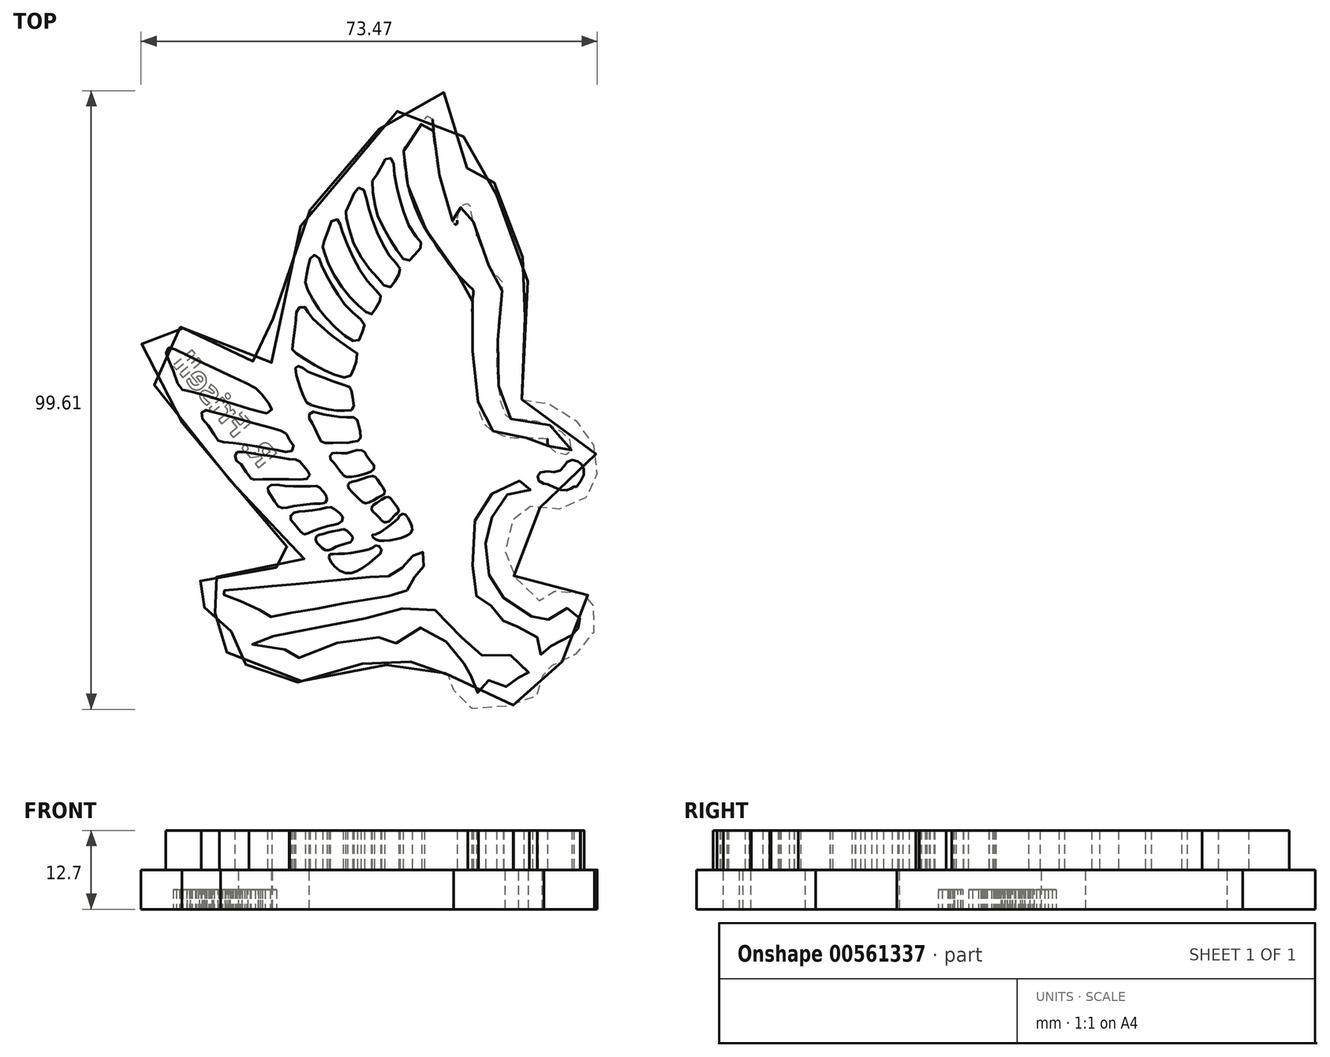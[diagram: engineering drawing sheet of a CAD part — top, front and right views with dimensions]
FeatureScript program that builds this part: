
annotation { "Feature Type Name" : "Feature", "Feature Type Description" : "" }
export const myFeature = defineFeature(function(context is Context, id is Id, definition is map)
    precondition{}
    {
        {
            var Q0;
            Q0=qCreatedBy(makeId("Top.planeOp"),FACE);
            var sketch = newSketch(context, id + "F0", { "sketchPlane" : qUnion([Q0])});
            skFitSpline(sketch, "E0", {"points": [v(-27.46, -3.62) * mm, v(-24.19, -4.03) * mm, v(-19.81, -6.13) * mm, v(-16.66, -9.45) * mm, v(-15.38, -13.42) * mm, v(-15.73, -17.22) * mm, v(-17.6, -19.78) * mm, v(-21.5, -21.24) * mm, v(-25.7, -20.83) * mm, v(-27.34, -21.24) * mm, v(-29.61, -24.4) * mm, v(-29.96, -29.3) * mm, v(-28.04, -32.85) * mm, v(-24.6, -36) * mm, v(-24.54, -35.89) * mm, v(-22.9, -34.72) * mm, v(-19.81, -34.37) * mm, v(-16.43, -35.36) * mm, v(-16.02, -36.35) * mm, v(-15.79, -38.75) * mm, v(-16.49, -42.6) * mm, v(-19.75, -45.17) * mm, v(-22.55, -46.45) * mm, v(-23.72, -46.8) * mm, v(-24.13, -47.8) * mm, v(-23.95, -49.48) * mm, v(-26, -52) * mm, v(-30.72, -53.1) * mm, v(-36.44, -53.16) * mm, v(-38.37, -50.53) * mm, v(-38.54, -48.43) * mm, v(-39.65, -47.8) * mm, v(-41.87, -45.75) * mm, v(-42.4, -44.82) * mm, v(-43.97, -45.05) * mm, v(-45.84, -46.1) * mm, v(-48.52, -46.57) * mm, v(-49.86, -46.1) * mm, v(-51.5, -46.04) * mm, v(-56.05, -46.45) * mm, v(-60.54, -47.67) * mm, v(-63.17, -49.02) * mm, v(-65.2, -48.96) * mm, v(-66.55, -47.73) * mm, v(-70.23, -46.97) * mm, v(-73.79, -45.17) * mm, v(-75.71, -43.47) * mm, v(-75.83, -41.9) * mm, v(-74.37, -40.96) * mm, v(-73.09, -40.44) * mm, v(-73.5, -39.62) * mm, v(-75.95, -38.4) * mm, v(-78.8, -37) * mm, v(-81.5, -35.3) * mm, v(-82.2, -33.96) * mm, v(-81.2, -33.38) * mm, v(-77.64, -32.39) * mm, v(-72.62, -31.45) * mm, v(-66.73, -30.64) * mm, v(-61.77, -29.94) * mm, v(-61.77, -29.76) * mm, v(-63.34, -28.77) * mm, v(-66.61, -25.97) * mm, v(-70.35, -21.12) * mm, v(-73.85, -17.27) * mm, v(-77.76, -12.72) * mm, v(-81.96, -7.53) * mm, v(-86.22, -2.1) * mm, v(-88.67, 5.2) * mm, v(-88.38, 8.17) * mm, v(-86.45, 9.16) * mm, v(-82.43, 8.05) * mm, v(-77.3, 5.72) * mm, v(-72.27, 3.27) * mm, v(-69, 2.04) * mm, v(-67.72, 2.4) * mm, v(-67.72, 4.78) * mm, v(-66.55, 15) * mm, v(-62.06, 26.14) * mm, v(-55.53, 34.55) * mm, v(-49.05, 41.37) * mm, v(-43.91, 45.45) * mm, v(-40.35, 45.98) * mm, v(-38.54, 44.29) * mm, v(-36.85, 38.8) * mm, v(-35.92, 32.03) * mm, v(-35.57, 32.2) * mm, v(-34.16, 34.37) * mm, v(-32.3, 32.56) * mm, v(-30.72, 25.09) * mm, v(-28.15, 20.25) * mm, v(-26.87, 18.73) * mm, v(-26.4, 17.74) * mm, v(-26.58, 14.59) * mm, v(-27.1, 7.53) * mm, v(-27.92, -0.47) * mm, v(-27.46, -3.62) * mm]});
            skSolve(sketch);
        }
        {
            var Q0;
            Q0 = qSketchRegion(id + "F0", true);
            extrude(context, id + "F1", {"entities" : qUnion([Q0]), "oppositeDirection" : true, "depth" : 6.35 * mm, "offsetDistance" : 25.4 * mm});
        }
        {
            var Q0;
            Q0=qCreatedBy(makeId("Top.planeOp"),FACE);
            var sketch = newSketch(context, id + "F2", { "sketchPlane" : qUnion([Q0])});
            skFitSpline(sketch, "E1", {"points": [v(-51.04, -25.31) * mm, v(-51.52, -25.35) * mm, v(-51.52, -25.66) * mm, v(-51.02, -26.1) * mm, v(-50.3, -26.34) * mm, v(-48.86, -26.31) * mm, v(-47.17, -25.97) * mm, v(-45.9, -25.5) * mm, v(-45.17, -24.78) * mm, v(-45.15, -24.02) * mm, v(-45.57, -23.09) * mm, v(-46.1, -22.25) * mm, v(-46.47, -22) * mm, v(-47.1, -22.22) * mm, v(-47.35, -22.7) * mm, v(-48.04, -23.34) * mm, v(-49.27, -24.27) * mm, v(-51.04, -25.31) * mm]});
            skFitSpline(sketch, "E2", {"points": [v(-50.45, -22.6) * mm, v(-49.82, -23.24) * mm, v(-49.4, -23.4) * mm, v(-48.9, -23.23) * mm, v(-48.23, -22.57) * mm, v(-47.83, -22.14) * mm, v(-47.45, -21.88) * mm, v(-47.28, -21.48) * mm, v(-47.79, -20.59) * mm, v(-48.48, -19.66) * mm, v(-48.92, -19.3) * mm, v(-49.42, -19.34) * mm, v(-51.03, -20.37) * mm, v(-51.5, -20.73) * mm, v(-51.69, -21.2) * mm, v(-51.41, -21.69) * mm, v(-50.45, -22.6) * mm]});
            skFitSpline(sketch, "E3", {"points": [v(-54.05, -16.7) * mm, v(-54.96, -16.88) * mm, v(-55.42, -17.2) * mm, v(-55.48, -17.65) * mm, v(-54.82, -18.46) * mm, v(-53.58, -19.71) * mm, v(-52.94, -20.23) * mm, v(-52.37, -20.3) * mm, v(-51.26, -19.77) * mm, v(-50.08, -19.1) * mm, v(-49.6, -18.83) * mm, v(-49.59, -18.2) * mm, v(-50.1, -17.36) * mm, v(-50.9, -16.28) * mm, v(-51.3, -15.92) * mm, v(-52.13, -16.03) * mm, v(-54.05, -16.7) * mm]});
            skFitSpline(sketch, "E4", {"points": [v(-57.72, -13.85) * mm, v(-56.93, -14.86) * mm, v(-56.26, -15.72) * mm, v(-55.94, -16.02) * mm, v(-55.52, -16.07) * mm, v(-53.9, -15.92) * mm, v(-52.14, -15.37) * mm, v(-51.39, -14.9) * mm, v(-51.2, -14.4) * mm, v(-51.52, -13.84) * mm, v(-52.48, -12.6) * mm, v(-52.8, -12.02) * mm, v(-53.23, -11.8) * mm, v(-54.23, -11.79) * mm, v(-55.3, -12.15) * mm, v(-56.3, -12.28) * mm, v(-57.4, -12.16) * mm, v(-58.09, -12.3) * mm, v(-58.3, -12.63) * mm, v(-58.28, -13.2) * mm, v(-57.72, -13.85) * mm]});
            skFitSpline(sketch, "E5", {"points": [v(-60.74, -8.34) * mm, v(-60, -9.95) * mm, v(-59.7, -10.42) * mm, v(-59, -10.58) * mm, v(-56.88, -10.55) * mm, v(-55.63, -10.57) * mm, v(-54.74, -10.42) * mm, v(-53.93, -10.3) * mm, v(-53.49, -9.95) * mm, v(-53.46, -8.76) * mm, v(-53.79, -7.67) * mm, v(-53.94, -6.97) * mm, v(-54.45, -6.5) * mm, v(-55.99, -6.45) * mm, v(-57.67, -6.27) * mm, v(-59.4, -6.02) * mm, v(-60.52, -5.7) * mm, v(-61.18, -5.58) * mm, v(-61.67, -5.94) * mm, v(-61.74, -6.5) * mm, v(-61.22, -7.41) * mm, v(-60.74, -8.34) * mm]});
            skFitSpline(sketch, "E6", {"points": [v(-63.17, -1.71) * mm, v(-62.41, -3.58) * mm, v(-61.93, -4.24) * mm, v(-60.58, -4.72) * mm, v(-58.33, -5.25) * mm, v(-56.8, -5.38) * mm, v(-55.13, -5.36) * mm, v(-54.57, -5.03) * mm, v(-54.67, -3.39) * mm, v(-54.87, -2.14) * mm, v(-55.05, -1.69) * mm, v(-56.2, -1.23) * mm, v(-58.7, -0.34) * mm, v(-60.9, 0.47) * mm, v(-62.36, 1.16) * mm, v(-62.93, 1.64) * mm, v(-63.62, 1.76) * mm, v(-63.88, 1.6) * mm, v(-63.87, 0.57) * mm, v(-63.37, -1.03) * mm, v(-63.17, -1.71) * mm]});
            skFitSpline(sketch, "E7", {"points": [v(-54.52, 1.42) * mm, v(-54.96, 0.35) * mm, v(-55.57, -0.04) * mm, v(-57.39, 0.32) * mm, v(-59.4, 1.18) * mm, v(-61.74, 2.53) * mm, v(-63.58, 3.67) * mm, v(-64.25, 4.2) * mm, v(-64.47, 4.66) * mm, v(-64.2, 6.39) * mm, v(-63.9, 8.7) * mm, v(-63.81, 10.1) * mm, v(-63.62, 10.9) * mm, v(-63.15, 11.33) * mm, v(-62.5, 11.33) * mm, v(-62.08, 10.92) * mm, v(-61.72, 10.1) * mm, v(-60.7, 9.02) * mm, v(-58.33, 6.9) * mm, v(-56.27, 5.4) * mm, v(-54.17, 3.97) * mm, v(-53.97, 3.78) * mm, v(-54.19, 2.21) * mm, v(-54.52, 1.42) * mm]});
            skFitSpline(sketch, "E8", {"points": [v(-53.17, 7.17) * mm, v(-53.61, 6.04) * mm, v(-54.24, 5.74) * mm, v(-55.3, 6.2) * mm, v(-57.23, 7.79) * mm, v(-59.49, 10.1) * mm, v(-60.67, 11.77) * mm, v(-61.78, 13.77) * mm, v(-62.3, 14.94) * mm, v(-62.29, 15.94) * mm, v(-62.03, 16.96) * mm, v(-61.75, 18.44) * mm, v(-61.5, 19.25) * mm, v(-60.98, 19.66) * mm, v(-60.31, 19.46) * mm, v(-59.98, 18.81) * mm, v(-59.58, 17.76) * mm, v(-58.35, 15.34) * mm, v(-57.3, 13.62) * mm, v(-56.03, 11.73) * mm, v(-54.32, 10.12) * mm, v(-53.09, 9.02) * mm, v(-52.83, 8.32) * mm, v(-53.17, 7.17) * mm]});
            skFitSpline(sketch, "E9", {"points": [v(-51.1, 10.94) * mm, v(-50.37, 12.28) * mm, v(-50.18, 12.7) * mm, v(-50.23, 13.17) * mm, v(-50.7, 13.7) * mm, v(-52.36, 15.53) * mm, v(-53.96, 17.96) * mm, v(-55.32, 20.76) * mm, v(-56.47, 23.7) * mm, v(-56.72, 24.63) * mm, v(-56.85, 25.12) * mm, v(-57.37, 25.47) * mm, v(-58.04, 25.24) * mm, v(-58.45, 24.13) * mm, v(-59.2, 22.13) * mm, v(-59.49, 21.57) * mm, v(-59.49, 20.61) * mm, v(-59.08, 19.57) * mm, v(-58.36, 17.67) * mm, v(-56.85, 15.13) * mm, v(-55.24, 12.97) * mm, v(-53.49, 11.25) * mm, v(-52.4, 10.4) * mm, v(-51.87, 10.1) * mm, v(-51.32, 10.43) * mm, v(-51.1, 10.94) * mm]});
            skFitSpline(sketch, "E10", {"points": [v(-47.94, 15.45) * mm, v(-48.57, 14.55) * mm, v(-49.36, 14.57) * mm, v(-50.53, 15.76) * mm, v(-52.54, 18.15) * mm, v(-54.84, 22.28) * mm, v(-55.66, 25.43) * mm, v(-55.86, 26.34) * mm, v(-55.25, 27.84) * mm, v(-54.36, 29.83) * mm, v(-53.78, 30.45) * mm, v(-53.22, 30.45) * mm, v(-52.64, 29.46) * mm, v(-52.2, 27.4) * mm, v(-51.34, 24.8) * mm, v(-49.85, 21.36) * mm, v(-48.27, 18.91) * mm, v(-47.28, 17.9) * mm, v(-47.06, 17.28) * mm, v(-47.25, 16.55) * mm, v(-47.94, 15.45) * mm]});
            skFitSpline(sketch, "E11", {"points": [v(-44.82, 19.6) * mm, v(-45.48, 18.86) * mm, v(-46.16, 18.78) * mm, v(-47.34, 20.09) * mm, v(-48.86, 22.43) * mm, v(-50.65, 25.95) * mm, v(-51.2, 28.1) * mm, v(-51.55, 31.43) * mm, v(-51.12, 32.12) * mm, v(-50.1, 33.9) * mm, v(-49.5, 34.98) * mm, v(-49, 35.37) * mm, v(-48.3, 35.06) * mm, v(-48.09, 33.9) * mm, v(-47.74, 31.23) * mm, v(-47.05, 28.49) * mm, v(-45.78, 24.66) * mm, v(-44.08, 22.13) * mm, v(-43.66, 21.62) * mm, v(-43.7, 20.98) * mm, v(-44.82, 19.6) * mm]});
            skFitSpline(sketch, "E12", {"points": [v(-52.13, -27.7) * mm, v(-51.3, -27.36) * mm, v(-50.95, -27.1) * mm, v(-50.4, -27.27) * mm, v(-50.06, -28) * mm, v(-50.76, -28.87) * mm, v(-53.08, -30.72) * mm, v(-54.62, -31.45) * mm, v(-56.24, -31.48) * mm, v(-57.8, -30.29) * mm, v(-58.44, -29.37) * mm, v(-58.43, -28.57) * mm, v(-58.1, -28.52) * mm, v(-57.08, -28.47) * mm, v(-55.42, -28.35) * mm, v(-53.4, -28) * mm, v(-52.13, -27.7) * mm]});
            skFitSpline(sketch, "E13", {"points": [v(-59.1, -27.87) * mm, v(-59.93, -27.2) * mm, v(-60.61, -26.42) * mm, v(-60.54, -25.66) * mm, v(-59.82, -25.33) * mm, v(-58.06, -24.88) * mm, v(-56.6, -24.57) * mm, v(-56.03, -24.51) * mm, v(-54.92, -25.42) * mm, v(-54.7, -26.04) * mm, v(-55.07, -26.56) * mm, v(-56.82, -27.1) * mm, v(-58.3, -27.8) * mm, v(-59.1, -27.87) * mm]});
            skFitSpline(sketch, "E14", {"points": [v(-64.2, -23.56) * mm, v(-64.74, -22.83) * mm, v(-64.53, -22.1) * mm, v(-63.6, -21.71) * mm, v(-62.07, -21.56) * mm, v(-59.49, -21.15) * mm, v(-58.3, -20.93) * mm, v(-57.58, -21.27) * mm, v(-56.4, -22.36) * mm, v(-56.32, -23) * mm, v(-57.05, -23.59) * mm, v(-58.24, -23.87) * mm, v(-60.5, -24.59) * mm, v(-61.96, -25.16) * mm, v(-62.58, -25.27) * mm, v(-63.47, -24.42) * mm, v(-64.2, -23.56) * mm]});
            skFitSpline(sketch, "E15", {"points": [v(-59.49, -18.43) * mm, v(-58.93, -19.13) * mm, v(-58.91, -19.95) * mm, v(-59.34, -20.3) * mm, v(-60.75, -20.38) * mm, v(-64.47, -20.82) * mm, v(-65.78, -21.1) * mm, v(-66.57, -20.9) * mm, v(-67.54, -19.53) * mm, v(-68.27, -18.45) * mm, v(-68.37, -17.85) * mm, v(-67.87, -17.38) * mm, v(-66.1, -17.44) * mm, v(-63.05, -17.59) * mm, v(-60.73, -17.53) * mm, v(-60.19, -17.62) * mm, v(-59.49, -18.43) * mm]});
            skFitSpline(sketch, "E16", {"points": [v(-62.65, -14.29) * mm, v(-61.82, -15.2) * mm, v(-61.6, -15.67) * mm, v(-61.93, -16.33) * mm, v(-63.34, -16.47) * mm, v(-67.87, -16.45) * mm, v(-70.59, -16.49) * mm, v(-70.9, -16.43) * mm, v(-71.67, -15.57) * mm, v(-73.02, -13.69) * mm, v(-73.56, -13.35) * mm, v(-73.6, -12.41) * mm, v(-73.33, -12.09) * mm, v(-72.21, -12.09) * mm, v(-70.23, -12.4) * mm, v(-67.5, -12.78) * mm, v(-64.98, -13.18) * mm, v(-63.81, -13.3) * mm, v(-63.2, -13.6) * mm, v(-62.65, -14.29) * mm]});
            skFitSpline(sketch, "E17", {"points": [v(-66.86, -11.75) * mm, v(-65.25, -12.05) * mm, v(-64.44, -11.83) * mm, v(-64.2, -11.1) * mm, v(-64.74, -10.33) * mm, v(-65.35, -9.23) * mm, v(-66.01, -8.7) * mm, v(-69, -7.84) * mm, v(-75.38, -6.1) * mm, v(-77.9, -5.42) * mm, v(-78.45, -5.3) * mm, v(-78.98, -5.67) * mm, v(-78.98, -6.55) * mm, v(-77.9, -7.91) * mm, v(-76.59, -9.92) * mm, v(-76.16, -10.34) * mm, v(-75.15, -10.48) * mm, v(-72.32, -10.83) * mm, v(-69.15, -11.33) * mm, v(-66.86, -11.75) * mm]});
            skFitSpline(sketch, "E18", {"points": [v(-71.26, -5.1) * mm, v(-69.41, -5.62) * mm, v(-68.8, -5.77) * mm, v(-68.08, -5.72) * mm, v(-67.74, -4.96) * mm, v(-68.4, -4.02) * mm, v(-69.62, -2.44) * mm, v(-70.41, -1.72) * mm, v(-73.4, -0.27) * mm, v(-78.14, 1.95) * mm, v(-81.45, 3.56) * mm, v(-83.67, 4.66) * mm, v(-84.3, 4.8) * mm, v(-84.78, 4.23) * mm, v(-84.68, 3.62) * mm, v(-84.27, 2.62) * mm, v(-83.21, 0) * mm, v(-82.48, -1.84) * mm, v(-81.73, -2.12) * mm, v(-79.25, -2.72) * mm, v(-75.51, -3.8) * mm, v(-71.26, -5.1) * mm]});
            skFitSpline(sketch, "E19", {"points": [v(-51.9, -32.16) * mm, v(-49.78, -31.97) * mm, v(-48.62, -32.03) * mm, v(-47.5, -31.38) * mm, v(-46.25, -30.15) * mm, v(-45.33, -29.06) * mm, v(-44.7, -28.4) * mm, v(-44.45, -28.05) * mm, v(-43.44, -28.15) * mm, v(-43.15, -29.26) * mm, v(-43.24, -30.4) * mm, v(-43.99, -31.1) * mm, v(-44.54, -31.89) * mm, v(-45.3, -33.4) * mm, v(-45.73, -34.15) * mm, v(-47.15, -34.94) * mm, v(-49.28, -35.3) * mm, v(-51.68, -35.67) * mm, v(-54.62, -36.17) * mm, v(-58.26, -36.85) * mm, v(-61.86, -37.5) * mm, v(-65.58, -38.12) * mm, v(-67.48, -38.58) * mm, v(-68.78, -38.43) * mm, v(-69.4, -37.77) * mm, v(-70.71, -36.92) * mm, v(-73.26, -35.91) * mm, v(-74.96, -35.2) * mm, v(-75.72, -34.96) * mm, v(-76.2, -34.69) * mm, v(-76, -34.48) * mm, v(-74.34, -34.3) * mm, v(-71.3, -33.99) * mm, v(-67.91, -33.63) * mm, v(-64.78, -33.4) * mm, v(-61.8, -33.1) * mm, v(-58.24, -32.8) * mm, v(-55.34, -32.52) * mm, v(-51.9, -32.16) * mm]});
            skFitSpline(sketch, "E20", {"points": [v(-57.2, -42.78) * mm, v(-60.6, -43.66) * mm, v(-62.93, -44.78) * mm, v(-63.64, -45.5) * mm, v(-64.47, -45.64) * mm, v(-64.94, -44.96) * mm, v(-64.9, -44.27) * mm, v(-65.6, -43.87) * mm, v(-67.43, -43.58) * mm, v(-68.9, -43.43) * mm, v(-70.85, -43.04) * mm, v(-71.4, -42.85) * mm, v(-71.11, -42.42) * mm, v(-69.85, -42.21) * mm, v(-66.92, -41.61) * mm, v(-62.68, -40.77) * mm, v(-59.49, -40.17) * mm, v(-57.71, -39.78) * mm, v(-53.85, -39.04) * mm, v(-50.18, -38.43) * mm, v(-48.23, -37.86) * mm, v(-46.69, -37.24) * mm, v(-45.94, -36.88) * mm, v(-43.05, -36.88) * mm, v(-41.55, -37.45) * mm, v(-39.52, -38.91) * mm, v(-37.97, -40.72) * mm, v(-37, -42.24) * mm, v(-36.7, -43.09) * mm, v(-36.08, -43.75) * mm, v(-34.46, -44.62) * mm, v(-33.1, -44.9) * mm, v(-31.57, -45.09) * mm, v(-30.1, -44.96) * mm, v(-28.85, -44.9) * mm, v(-27.26, -45.83) * mm, v(-27.08, -46.6) * mm, v(-26.7, -47.13) * mm, v(-26.34, -47.69) * mm, v(-26.35, -48.7) * mm, v(-26.76, -49.18) * mm, v(-27.4, -49.05) * mm, v(-27.67, -48.51) * mm, v(-28.16, -48.42) * mm, v(-28.8, -48.82) * mm, v(-28.8, -49.47) * mm, v(-28.95, -49.94) * mm, v(-29.7, -50.15) * mm, v(-30.09, -49.73) * mm, v(-30.62, -49.72) * mm, v(-31.2, -49.76) * mm, v(-32.07, -48.95) * mm, v(-32.59, -48.64) * mm, v(-32.95, -49.02) * mm, v(-33.45, -49.57) * mm, v(-33.84, -49.75) * mm, v(-34.36, -49.85) * mm, v(-34.47, -50.33) * mm, v(-34.49, -50.74) * mm, v(-35.27, -50.79) * mm, v(-35.97, -50.1) * mm, v(-36.15, -49.42) * mm, v(-35.95, -48.51) * mm, v(-35.33, -47.86) * mm, v(-34.9, -47.52) * mm, v(-34.77, -46.97) * mm, v(-35.53, -46.47) * mm, v(-36.78, -46.06) * mm, v(-38.11, -45.33) * mm, v(-38.86, -44.66) * mm, v(-39.28, -43.35) * mm, v(-40.2, -41.77) * mm, v(-41.49, -40.7) * mm, v(-42.84, -40.31) * mm, v(-44.23, -40.46) * mm, v(-45.76, -41.29) * mm, v(-47.03, -42.26) * mm, v(-47.53, -42.8) * mm, v(-48.18, -42.85) * mm, v(-48.57, -42.73) * mm, v(-48.67, -42.15) * mm, v(-48.73, -41.94) * mm, v(-49.2, -41.89) * mm, v(-52.13, -41.97) * mm, v(-55.2, -42.36) * mm, v(-57.2, -42.78) * mm]});
            skFitSpline(sketch, "E21", {"points": [v(-23.12, -11.1) * mm, v(-22.54, -11.77) * mm, v(-21.24, -12.36) * mm, v(-19.9, -12.38) * mm, v(-19.52, -11.97) * mm, v(-19.53, -10.54) * mm, v(-20.37, -9.4) * mm, v(-22.08, -8.17) * mm, v(-24.4, -7.29) * mm, v(-26.84, -6.87) * mm, v(-28.9, -6.73) * mm, v(-29.82, -6.6) * mm, v(-29.97, -6.33) * mm, v(-30.84, -4.01) * mm, v(-31.25, -0.8) * mm, v(-31.5, 1.72) * mm, v(-31.4, 5.23) * mm, v(-31.22, 8.54) * mm, v(-30.8, 12.5) * mm, v(-30.54, 14.63) * mm, v(-30.45, 15.19) * mm, v(-30.72, 15.57) * mm, v(-32.24, 17.1) * mm, v(-33.22, 18.96) * mm, v(-34.5, 22.38) * mm, v(-35.32, 25.2) * mm, v(-35.64, 26.83) * mm, v(-35.77, 27.58) * mm, v(-36.38, 27.88) * mm, v(-37.16, 27.5) * mm, v(-37.62, 26.71) * mm, v(-37.87, 25.49) * mm, v(-37.88, 24.83) * mm, v(-38.03, 24.59) * mm, v(-38.46, 24.88) * mm, v(-39.09, 26.54) * mm, v(-40.05, 29.8) * mm, v(-40.98, 33.57) * mm, v(-41.39, 36.87) * mm, v(-41.6, 38.89) * mm, v(-41.82, 41.23) * mm, v(-41.95, 41.6) * mm, v(-42.6, 41.95) * mm, v(-43, 41.74) * mm, v(-43.83, 40.46) * mm, v(-45.26, 38.52) * mm, v(-46.33, 37.09) * mm, v(-46.5, 36.93) * mm, v(-46.53, 36.01) * mm, v(-46.46, 34.32) * mm, v(-46.24, 32.42) * mm, v(-45.8, 30.8) * mm, v(-44.93, 28.11) * mm, v(-43.5, 24.84) * mm, v(-41.31, 21.32) * mm, v(-38.6, 17.49) * mm, v(-36.72, 15.42) * mm, v(-35.4, 14.13) * mm, v(-35.29, 14) * mm, v(-35.35, 12.93) * mm, v(-35.5, 9.8) * mm, v(-35.54, 6.7) * mm, v(-35.33, 2.59) * mm, v(-35.14, 0.6) * mm, v(-34.43, -4.5) * mm, v(-34.21, -5.92) * mm, v(-33.52, -7.42) * mm, v(-32.34, -8.53) * mm, v(-30.56, -9.37) * mm, v(-29.08, -9.75) * mm, v(-27.6, -9.76) * mm, v(-25.37, -9.78) * mm, v(-23.57, -9.87) * mm, v(-23.37, -9.94) * mm, v(-23.34, -10.57) * mm, v(-23.12, -11.1) * mm]});
            skFitSpline(sketch, "E22", {"points": [v(-23.19, -15.18) * mm, v(-22.06, -15.25) * mm, v(-20.9, -14.7) * mm, v(-20.32, -13.85) * mm, v(-19.4, -13.34) * mm, v(-18.4, -13.64) * mm, v(-17.76, -14.17) * mm, v(-17.45, -15.08) * mm, v(-17.76, -16.27) * mm, v(-18.66, -17.63) * mm, v(-18.84, -17.72) * mm, v(-19.31, -17.66) * mm, v(-19.68, -18.08) * mm, v(-20.54, -18.21) * mm, v(-21.78, -17.99) * mm, v(-23.44, -17.18) * mm, v(-24.05, -17.1) * mm, v(-24.9, -16.5) * mm, v(-24.83, -15.77) * mm, v(-24.39, -15.27) * mm, v(-23.7, -15.2) * mm, v(-23.19, -15.18) * mm]});
            skFitSpline(sketch, "E23", {"points": [v(-29.83, -18.94) * mm, v(-28.47, -18.23) * mm, v(-26.6, -18.15) * mm, v(-25.96, -18.12) * mm, v(-25.76, -17.8) * mm, v(-26.62, -17.1) * mm, v(-27.43, -16.7) * mm, v(-29.36, -17.1) * mm, v(-31.35, -18.17) * mm, v(-33.63, -19.93) * mm, v(-34.86, -22.37) * mm, v(-35.32, -25.48) * mm, v(-35.44, -31.3) * mm, v(-35.38, -32.7) * mm, v(-34.68, -35.46) * mm, v(-34.1, -36.2) * mm, v(-33.32, -36.75) * mm, v(-32.52, -36.8) * mm, v(-31.93, -37.33) * mm, v(-30.47, -38.57) * mm, v(-30.42, -38.75) * mm, v(-30.47, -39.3) * mm, v(-29.9, -40.14) * mm, v(-28.9, -40.33) * mm, v(-28.4, -40.1) * mm, v(-27.9, -40.37) * mm, v(-26.87, -41.2) * mm, v(-25.2, -41.85) * mm, v(-24.9, -42.03) * mm, v(-24.93, -43.07) * mm, v(-24.93, -43.85) * mm, v(-24.45, -44.68) * mm, v(-23.8, -44.53) * mm, v(-23.32, -44.04) * mm, v(-23.2, -43.4) * mm, v(-23.09, -43.33) * mm, v(-22.18, -43.17) * mm, v(-20.17, -42.36) * mm, v(-19.6, -41.66) * mm, v(-19.3, -41.51) * mm, v(-18.78, -41.68) * mm, v(-18.2, -41.42) * mm, v(-18.1, -40.85) * mm, v(-18.62, -40.21) * mm, v(-18.97, -39.96) * mm, v(-18.97, -39.23) * mm, v(-18.5, -39.01) * mm, v(-18.11, -38.84) * mm, v(-18, -38.11) * mm, v(-18.14, -37.74) * mm, v(-19.53, -37.33) * mm, v(-21.18, -37.16) * mm, v(-22.39, -37.8) * mm, v(-23.19, -39.04) * mm, v(-23.32, -39.89) * mm, v(-23.57, -39.83) * mm, v(-24.48, -39.34) * mm, v(-27.14, -37.8) * mm, v(-27.12, -37.81) * mm, v(-30.3, -35.65) * mm, v(-31.64, -34.4) * mm, v(-32.52, -32.62) * mm, v(-33.03, -30.31) * mm, v(-33.34, -27.74) * mm, v(-33.06, -25.1) * mm, v(-32.72, -23.66) * mm, v(-32, -21.97) * mm, v(-30.93, -20.1) * mm, v(-29.83, -18.94) * mm]});
            skSolve(sketch);
        }
        {
            var Q0;
            Q0 = qSketchRegion(id + "F2", true);
            extrude(context, id + "F3", {"entities" : qUnion([Q0]), "operationType" : NewBodyOperationType.ADD, "depth" : 6.35 * mm, "offsetDistance" : 25.4 * mm});
        }
        {
            var Q0;
            Q0=makeQuery(id+"F1.opExtrude","CAP_FACE",FACE,{"disambiguationData":[OSD([sQuery(id+"F0.wireOp",EDGE,"E0")])],"isStart":false});
            var sketch = newSketch(context, id + "F4", { "sketchPlane" : qUnion([Q0])});
            skText(sketch, "E24", { "text": "R. Frisell", "fontName": "OpenSans-Bold.ttf"});
            const initialGuessF4  = {"E24": [-0.06957, 0.01495, -0.64279, -0.76604, 0.00381]};
            skSetInitialGuess(sketch, initialGuessF4);
            skSolve(sketch);
        }
        {
            var Q0;
            Q0 = qSketchRegion(id + "F4", true);
            extrude(context, id + "F5", {"entities" : qUnion([Q0]), "operationType" : NewBodyOperationType.REMOVE, "oppositeDirection" : true, "depth" : 3.17 * mm, "offsetDistance" : 25.4 * mm});
        }
    });
